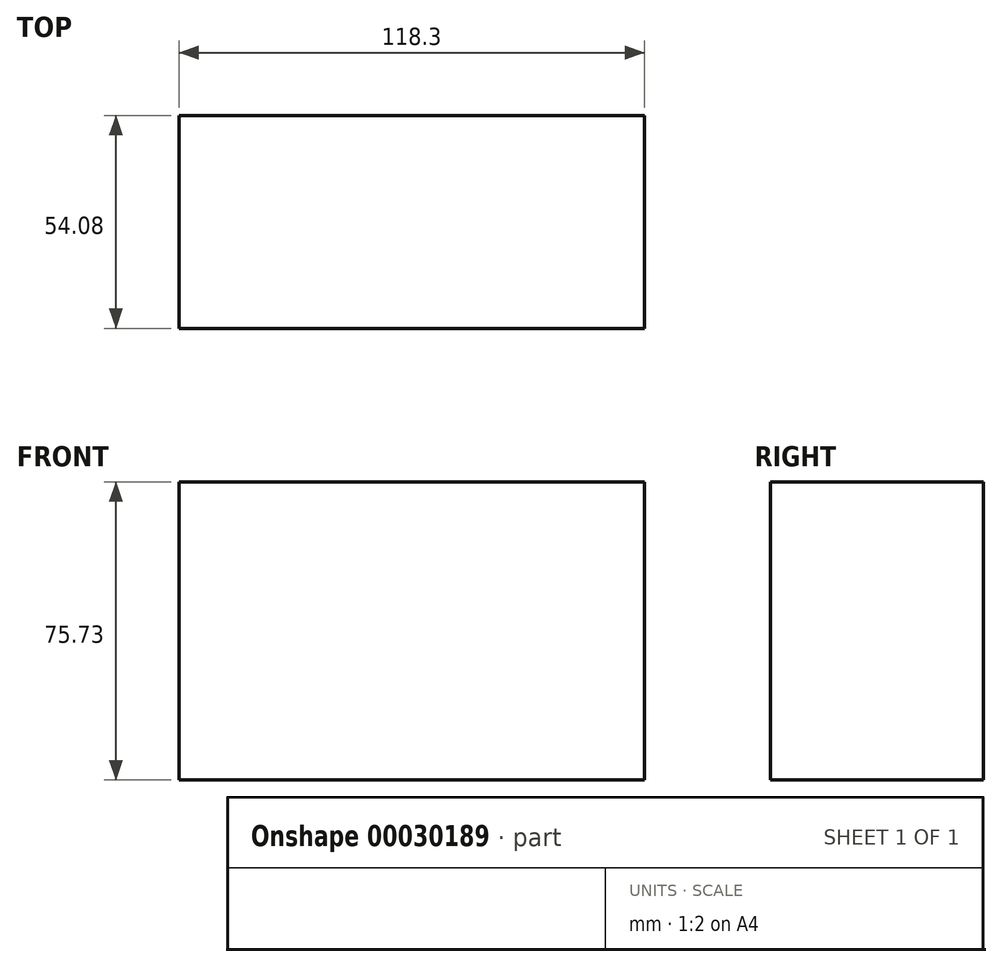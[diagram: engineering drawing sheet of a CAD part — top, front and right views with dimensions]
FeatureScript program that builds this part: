
annotation { "Feature Type Name" : "Feature", "Feature Type Description" : "" }
export const myFeature = defineFeature(function(context is Context, id is Id, definition is map)
    precondition{}
    {
        {
            var Q0;
            Q0=qCreatedBy(makeId("Top.planeOp"),FACE);
            var sketch = newSketch(context, id + "F0", { "sketchPlane" : qUnion([Q0])});
            skLineSegment(sketch, "E0.bottom", {"start": v(0, 0) * mm, "end": v(-118.3, 0) * mm});
            skLineSegment(sketch, "E0.top", {"start": v(0, 54.08) * mm, "end": v(-118.3, 54.08) * mm});
            skLineSegment(sketch, "E0.left", {"start": v(0, 0) * mm, "end": v(0, 54.08) * mm});
            skLineSegment(sketch, "E0.right", {"start": v(-118.3, 0) * mm, "end": v(-118.3, 54.08) * mm});
            skSolve(sketch);
        }
        {
            var Q0;
            Q0=makeQuery(id+"F0.imprint","IMPRINT",FACE,{"disambiguationData":[TD([[makeQuery(id+"F0.imprint","IMPRINT",EDGE,{"derivedFrom":sQuery(id+"F0.wireOp",EDGE,"E0.bottom")}),-1.0]])]});
            extrude(context, id + "F1", {"entities" : qUnion([Q0]), "depth" : 75.73 * mm});
        }
    });
